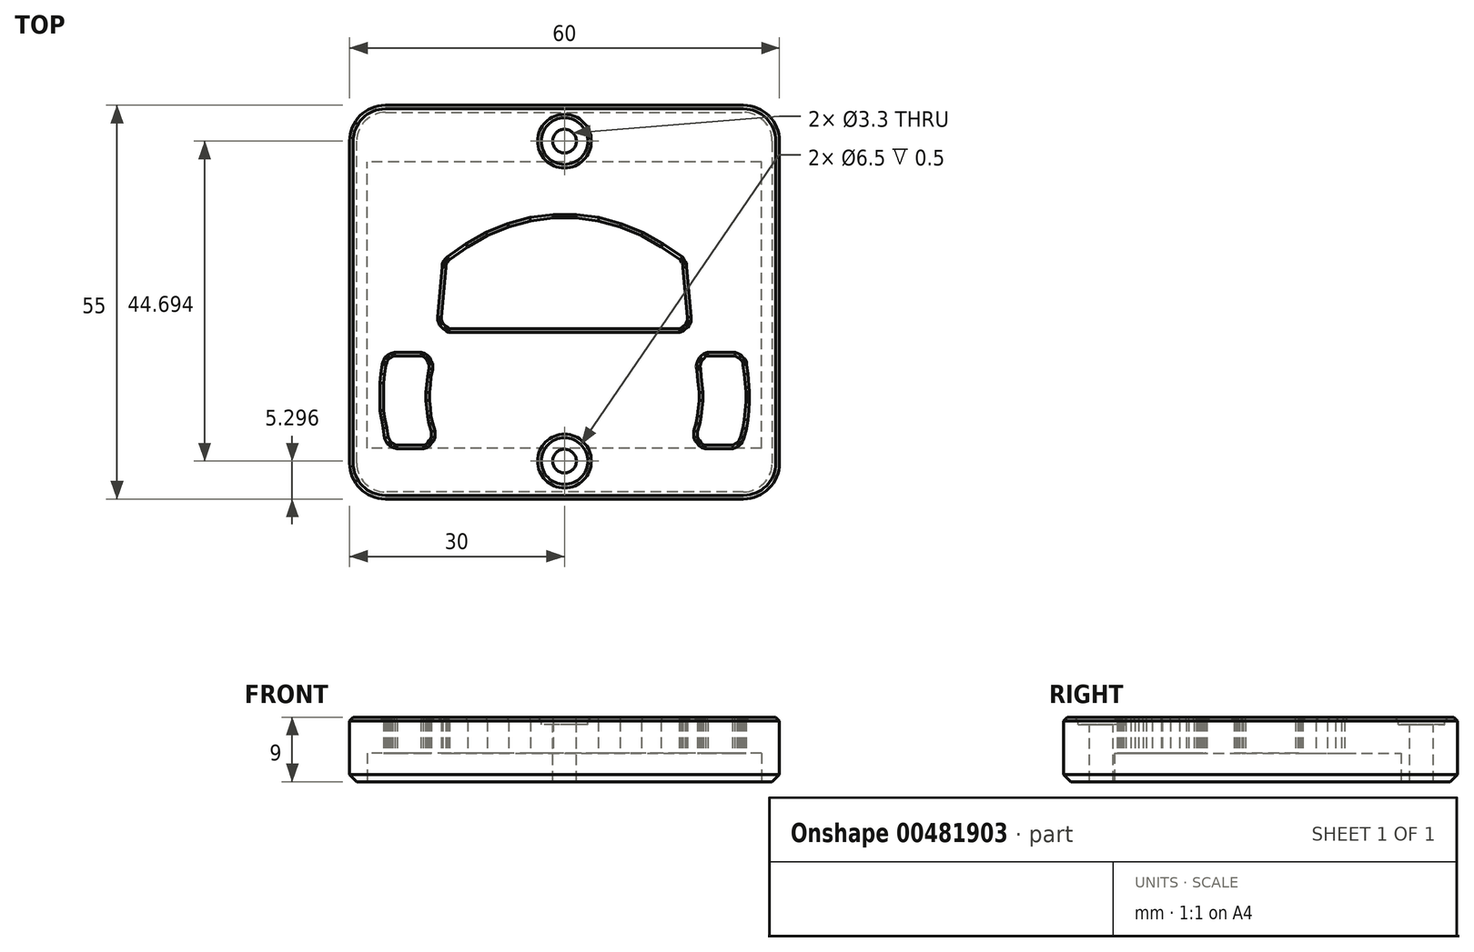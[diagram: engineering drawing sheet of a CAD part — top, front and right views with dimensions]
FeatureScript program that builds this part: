
annotation { "Feature Type Name" : "Feature", "Feature Type Description" : "" }
export const myFeature = defineFeature(function(context is Context, id is Id, definition is map)
    precondition{}
    {
        {
            var Q0;
            Q0=qCreatedBy(makeId("Top.planeOp"),FACE);
            var sketch = newSketch(context, id + "F0", { "sketchPlane" : qUnion([Q0])});
            skLineSegment(sketch, "E0.bottom", {"start": v(30, -27.5) * mm, "end": v(-30, -27.5) * mm});
            skLineSegment(sketch, "E0.top", {"start": v(30, 27.5) * mm, "end": v(-30, 27.5) * mm});
            skLineSegment(sketch, "E0.left", {"start": v(30, -27.5) * mm, "end": v(30, 27.5) * mm});
            skLineSegment(sketch, "E0.right", {"start": v(-30, -27.5) * mm, "end": v(-30, 27.5) * mm});
            skPoint(sketch, "E0.middle", {"position": v(0, 0) * mm});
            skSolve(sketch);
        }
        {
            var Q0;
            Q0 = qSketchRegion(id + "F0", true);
            extrude(context, id + "F1", {"entities" : qUnion([Q0]), "depth" : 9 * mm});
        }
        {
            var Q0;
            Q0=qCreatedBy(makeId("Top.planeOp"),FACE);
            var sketch = newSketch(context, id + "F2", { "sketchPlane" : qUnion([Q0])});
            skPoint(sketch, "E1.middle", {"position": v(0, 0) * mm});
            skLineSegment(sketch, "E2.bottom", {"start": v(27.48, -20.4) * mm, "end": v(-27.52, -20.4) * mm});
            skLineSegment(sketch, "E2.top", {"start": v(27.48, 19.6) * mm, "end": v(-27.52, 19.6) * mm});
            skLineSegment(sketch, "E2.left", {"start": v(27.48, -20.4) * mm, "end": v(27.48, 19.6) * mm});
            skLineSegment(sketch, "E2.right", {"start": v(-27.52, -20.4) * mm, "end": v(-27.52, 19.6) * mm});
            skPoint(sketch, "E2.middle", {"position": v(-0.02, -0.4) * mm});
            skSolve(sketch);
        }
        {
            var Q0;
            Q0 = qSketchRegion(id + "F2", true);
            extrude(context, id + "F3", {"entities" : qUnion([Q0]), "operationType" : NewBodyOperationType.REMOVE, "depth" : 4 * mm});
        }
        {
            var Q0;
            Q0=qCreatedBy(makeId("Top.planeOp"),FACE);
            var sketch = newSketch(context, id + "F4", { "sketchPlane" : qUnion([Q0])});
            skLineSegment(sketch, "E3", {"start": v(23.1, -20) * mm, "end": v(20.03, -20) * mm});
            skLineSegment(sketch, "E4", {"start": v(20.03, -20) * mm, "end": v(19.71, -20) * mm});
            skLineSegment(sketch, "E5", {"start": v(19.71, -20) * mm, "end": v(19.4, -19.89) * mm});
            skLineSegment(sketch, "E6", {"start": v(19.4, -19.89) * mm, "end": v(19.08, -19.68) * mm});
            skLineSegment(sketch, "E7", {"start": v(19.08, -19.68) * mm, "end": v(18.87, -19.36) * mm});
            skLineSegment(sketch, "E8", {"start": v(18.87, -19.36) * mm, "end": v(18.66, -19.15) * mm});
            skLineSegment(sketch, "E9", {"start": v(18.66, -19.15) * mm, "end": v(18.55, -18.83) * mm});
            skLineSegment(sketch, "E10", {"start": v(18.55, -18.83) * mm, "end": v(18.55, -18.4) * mm});
            skLineSegment(sketch, "E11", {"start": v(18.55, -18.4) * mm, "end": v(18.55, -18.1) * mm});
            skLineSegment(sketch, "E12", {"start": v(18.55, -18.1) * mm, "end": v(18.87, -17.03) * mm});
            skLineSegment(sketch, "E13", {"start": v(18.87, -17.03) * mm, "end": v(19.08, -15.97) * mm});
            skLineSegment(sketch, "E14", {"start": v(19.08, -15.97) * mm, "end": v(19.19, -14.8) * mm});
            skLineSegment(sketch, "E15", {"start": v(19.19, -14.8) * mm, "end": v(19.3, -13.75) * mm});
            skLineSegment(sketch, "E16", {"start": v(19.3, -13.75) * mm, "end": v(19.3, -12.59) * mm});
            skLineSegment(sketch, "E17", {"start": v(19.3, -12.59) * mm, "end": v(19.19, -11.53) * mm});
            skLineSegment(sketch, "E18", {"start": v(19.19, -11.53) * mm, "end": v(19.08, -10.37) * mm});
            skLineSegment(sketch, "E19", {"start": v(19.08, -10.37) * mm, "end": v(18.97, -9.3) * mm});
            skLineSegment(sketch, "E20", {"start": v(18.97, -9.3) * mm, "end": v(18.87, -8.99) * mm});
            skLineSegment(sketch, "E21", {"start": v(18.87, -8.99) * mm, "end": v(18.97, -8.67) * mm});
            skLineSegment(sketch, "E22", {"start": v(18.97, -8.67) * mm, "end": v(19.08, -8.36) * mm});
            skLineSegment(sketch, "E23", {"start": v(19.08, -8.36) * mm, "end": v(19.3, -8.04) * mm});
            skLineSegment(sketch, "E24", {"start": v(19.3, -8.04) * mm, "end": v(19.5, -7.83) * mm});
            skLineSegment(sketch, "E25", {"start": v(19.5, -7.83) * mm, "end": v(19.71, -7.61) * mm});
            skLineSegment(sketch, "E26", {"start": v(19.71, -7.61) * mm, "end": v(20.03, -7.5) * mm});
            skLineSegment(sketch, "E27", {"start": v(20.03, -7.5) * mm, "end": v(20.35, -7.5) * mm});
            skLineSegment(sketch, "E28", {"start": v(20.35, -7.5) * mm, "end": v(23.42, -7.5) * mm});
            skLineSegment(sketch, "E29", {"start": v(23.42, -7.5) * mm, "end": v(23.74, -7.5) * mm});
            skLineSegment(sketch, "E30", {"start": v(23.74, -7.5) * mm, "end": v(23.95, -7.61) * mm});
            skLineSegment(sketch, "E31", {"start": v(23.95, -7.61) * mm, "end": v(24.16, -7.72) * mm});
            skLineSegment(sketch, "E32", {"start": v(24.16, -7.72) * mm, "end": v(24.37, -7.83) * mm});
            skLineSegment(sketch, "E33", {"start": v(24.37, -7.83) * mm, "end": v(24.58, -8.04) * mm});
            skLineSegment(sketch, "E34", {"start": v(24.58, -8.04) * mm, "end": v(24.8, -8.25) * mm});
            skLineSegment(sketch, "E35", {"start": v(24.8, -8.25) * mm, "end": v(24.9, -8.46) * mm});
            skLineSegment(sketch, "E36", {"start": v(24.9, -8.46) * mm, "end": v(24.9, -8.78) * mm});
            skLineSegment(sketch, "E37", {"start": v(24.9, -8.78) * mm, "end": v(25.11, -10.05) * mm});
            skLineSegment(sketch, "E38", {"start": v(25.11, -10.05) * mm, "end": v(25.22, -11.32) * mm});
            skLineSegment(sketch, "E39", {"start": v(25.22, -11.32) * mm, "end": v(25.32, -12.59) * mm});
            skLineSegment(sketch, "E40", {"start": v(25.32, -12.59) * mm, "end": v(25.32, -13.86) * mm});
            skLineSegment(sketch, "E41", {"start": v(25.32, -13.86) * mm, "end": v(25.22, -15.13) * mm});
            skLineSegment(sketch, "E42", {"start": v(25.22, -15.13) * mm, "end": v(25.11, -16.4) * mm});
            skLineSegment(sketch, "E43", {"start": v(25.11, -16.4) * mm, "end": v(24.9, -17.56) * mm});
            skLineSegment(sketch, "E44", {"start": v(24.9, -17.56) * mm, "end": v(24.58, -18.83) * mm});
            skLineSegment(sketch, "E45", {"start": v(24.58, -18.83) * mm, "end": v(24.48, -19.04) * mm});
            skLineSegment(sketch, "E46", {"start": v(24.48, -19.04) * mm, "end": v(24.37, -19.25) * mm});
            skLineSegment(sketch, "E47", {"start": v(24.37, -19.25) * mm, "end": v(24.26, -19.47) * mm});
            skLineSegment(sketch, "E48", {"start": v(24.26, -19.47) * mm, "end": v(24.05, -19.68) * mm});
            skLineSegment(sketch, "E49", {"start": v(24.05, -19.68) * mm, "end": v(23.84, -19.78) * mm});
            skLineSegment(sketch, "E50", {"start": v(23.84, -19.78) * mm, "end": v(23.63, -19.89) * mm});
            skLineSegment(sketch, "E51", {"start": v(23.63, -19.89) * mm, "end": v(23.42, -20) * mm});
            skLineSegment(sketch, "E52", {"start": v(23.42, -20) * mm, "end": v(23.1, -20) * mm});
            skLineSegment(sketch, "E53", {"start": v(-23.46, -7.5) * mm, "end": v(-20.4, -7.5) * mm});
            skLineSegment(sketch, "E54", {"start": v(-20.4, -7.5) * mm, "end": v(-20.07, -7.5) * mm});
            skLineSegment(sketch, "E55", {"start": v(-20.07, -7.5) * mm, "end": v(-19.76, -7.61) * mm});
            skLineSegment(sketch, "E56", {"start": v(-19.76, -7.61) * mm, "end": v(-19.44, -7.83) * mm});
            skLineSegment(sketch, "E57", {"start": v(-19.44, -7.83) * mm, "end": v(-19.23, -8.04) * mm});
            skLineSegment(sketch, "E58", {"start": v(-19.23, -8.04) * mm, "end": v(-19.12, -8.36) * mm});
            skLineSegment(sketch, "E59", {"start": v(-19.12, -8.36) * mm, "end": v(-18.9, -8.67) * mm});
            skLineSegment(sketch, "E60", {"start": v(-18.9, -8.67) * mm, "end": v(-18.9, -8.99) * mm});
            skLineSegment(sketch, "E61", {"start": v(-18.9, -8.99) * mm, "end": v(-18.9, -9.3) * mm});
            skLineSegment(sketch, "E62", {"start": v(-18.9, -9.3) * mm, "end": v(-19.12, -10.37) * mm});
            skLineSegment(sketch, "E63", {"start": v(-19.12, -10.37) * mm, "end": v(-19.23, -11.53) * mm});
            skLineSegment(sketch, "E64", {"start": v(-19.23, -11.53) * mm, "end": v(-19.33, -12.59) * mm});
            skLineSegment(sketch, "E65", {"start": v(-19.33, -12.59) * mm, "end": v(-19.33, -13.75) * mm});
            skLineSegment(sketch, "E66", {"start": v(-19.33, -13.75) * mm, "end": v(-19.23, -14.8) * mm});
            skLineSegment(sketch, "E67", {"start": v(-19.23, -14.8) * mm, "end": v(-19.12, -15.97) * mm});
            skLineSegment(sketch, "E68", {"start": v(-19.12, -15.97) * mm, "end": v(-18.9, -17.03) * mm});
            skLineSegment(sketch, "E69", {"start": v(-18.9, -17.03) * mm, "end": v(-18.6, -18.1) * mm});
            skLineSegment(sketch, "E70", {"start": v(-18.6, -18.1) * mm, "end": v(-18.6, -18.4) * mm});
            skLineSegment(sketch, "E71", {"start": v(-18.6, -18.4) * mm, "end": v(-18.6, -18.83) * mm});
            skLineSegment(sketch, "E72", {"start": v(-18.6, -18.83) * mm, "end": v(-18.7, -19.15) * mm});
            skLineSegment(sketch, "E73", {"start": v(-18.7, -19.15) * mm, "end": v(-18.9, -19.36) * mm});
            skLineSegment(sketch, "E74", {"start": v(-18.9, -19.36) * mm, "end": v(-19.12, -19.68) * mm});
            skLineSegment(sketch, "E75", {"start": v(-19.12, -19.68) * mm, "end": v(-19.44, -19.89) * mm});
            skLineSegment(sketch, "E76", {"start": v(-19.44, -19.89) * mm, "end": v(-19.76, -20) * mm});
            skLineSegment(sketch, "E77", {"start": v(-19.76, -20) * mm, "end": v(-20.07, -20) * mm});
            skLineSegment(sketch, "E78", {"start": v(-20.07, -20) * mm, "end": v(-23.14, -20) * mm});
            skLineSegment(sketch, "E79", {"start": v(-23.14, -20) * mm, "end": v(-23.35, -20) * mm});
            skLineSegment(sketch, "E80", {"start": v(-23.35, -20) * mm, "end": v(-23.67, -19.89) * mm});
            skLineSegment(sketch, "E81", {"start": v(-23.67, -19.89) * mm, "end": v(-23.88, -19.78) * mm});
            skLineSegment(sketch, "E82", {"start": v(-23.88, -19.78) * mm, "end": v(-24.1, -19.68) * mm});
            skLineSegment(sketch, "E83", {"start": v(-24.1, -19.68) * mm, "end": v(-24.3, -19.47) * mm});
            skLineSegment(sketch, "E84", {"start": v(-24.3, -19.47) * mm, "end": v(-24.41, -19.25) * mm});
            skLineSegment(sketch, "E85", {"start": v(-24.41, -19.25) * mm, "end": v(-24.52, -19.04) * mm});
            skLineSegment(sketch, "E86", {"start": v(-24.52, -19.04) * mm, "end": v(-24.62, -18.83) * mm});
            skLineSegment(sketch, "E87", {"start": v(-24.62, -18.83) * mm, "end": v(-24.83, -17.56) * mm});
            skLineSegment(sketch, "E88", {"start": v(-24.83, -17.56) * mm, "end": v(-25.05, -16.4) * mm});
            skLineSegment(sketch, "E89", {"start": v(-25.05, -16.4) * mm, "end": v(-25.26, -15.13) * mm});
            skLineSegment(sketch, "E90", {"start": v(-25.26, -15.13) * mm, "end": v(-25.26, -13.86) * mm});
            skLineSegment(sketch, "E91", {"start": v(-25.26, -13.86) * mm, "end": v(-25.26, -12.59) * mm});
            skLineSegment(sketch, "E92", {"start": v(-25.26, -12.59) * mm, "end": v(-25.26, -11.32) * mm});
            skLineSegment(sketch, "E93", {"start": v(-25.26, -11.32) * mm, "end": v(-25.15, -10.05) * mm});
            skLineSegment(sketch, "E94", {"start": v(-25.15, -10.05) * mm, "end": v(-24.94, -8.78) * mm});
            skLineSegment(sketch, "E95", {"start": v(-24.94, -8.78) * mm, "end": v(-24.83, -8.46) * mm});
            skLineSegment(sketch, "E96", {"start": v(-24.83, -8.46) * mm, "end": v(-24.73, -8.25) * mm});
            skLineSegment(sketch, "E97", {"start": v(-24.73, -8.25) * mm, "end": v(-24.62, -8.04) * mm});
            skLineSegment(sketch, "E98", {"start": v(-24.62, -8.04) * mm, "end": v(-24.41, -7.83) * mm});
            skLineSegment(sketch, "E99", {"start": v(-24.41, -7.83) * mm, "end": v(-24.2, -7.72) * mm});
            skLineSegment(sketch, "E100", {"start": v(-24.2, -7.72) * mm, "end": v(-23.99, -7.61) * mm});
            skLineSegment(sketch, "E101", {"start": v(-23.99, -7.61) * mm, "end": v(-23.67, -7.5) * mm});
            skLineSegment(sketch, "E102", {"start": v(-23.67, -7.5) * mm, "end": v(-23.46, -7.5) * mm});
            skLineSegment(sketch, "E103", {"start": v(-17.22, -2.11) * mm, "end": v(-16.58, 4.87) * mm});
            skLineSegment(sketch, "E104", {"start": v(-16.58, 4.87) * mm, "end": v(-16.58, 4.98) * mm});
            skLineSegment(sketch, "E105", {"start": v(-16.58, 4.98) * mm, "end": v(-16.58, 5.19) * mm});
            skLineSegment(sketch, "E106", {"start": v(-16.58, 5.19) * mm, "end": v(-16.48, 5.3) * mm});
            skLineSegment(sketch, "E107", {"start": v(-16.48, 5.3) * mm, "end": v(-16.48, 5.4) * mm});
            skLineSegment(sketch, "E108", {"start": v(-16.48, 5.4) * mm, "end": v(-16.37, 5.5) * mm});
            skLineSegment(sketch, "E109", {"start": v(-16.37, 5.5) * mm, "end": v(-16.26, 5.72) * mm});
            skLineSegment(sketch, "E110", {"start": v(-16.26, 5.72) * mm, "end": v(-16.16, 5.82) * mm});
            skLineSegment(sketch, "E111", {"start": v(-16.16, 5.82) * mm, "end": v(-16.05, 5.93) * mm});
            skLineSegment(sketch, "E112", {"start": v(-16.05, 5.93) * mm, "end": v(-13.51, 7.73) * mm});
            skLineSegment(sketch, "E113", {"start": v(-13.51, 7.73) * mm, "end": v(-10.76, 9.32) * mm});
            skLineSegment(sketch, "E114", {"start": v(-10.76, 9.32) * mm, "end": v(-7.8, 10.48) * mm});
            skLineSegment(sketch, "E115", {"start": v(-7.8, 10.48) * mm, "end": v(-4.73, 11.33) * mm});
            skLineSegment(sketch, "E116", {"start": v(-4.73, 11.33) * mm, "end": v(-1.56, 11.75) * mm});
            skLineSegment(sketch, "E117", {"start": v(-1.56, 11.75) * mm, "end": v(1.62, 11.75) * mm});
            skLineSegment(sketch, "E118", {"start": v(1.62, 11.75) * mm, "end": v(4.69, 11.33) * mm});
            skLineSegment(sketch, "E119", {"start": v(4.69, 11.33) * mm, "end": v(7.76, 10.48) * mm});
            skLineSegment(sketch, "E120", {"start": v(7.76, 10.48) * mm, "end": v(10.72, 9.32) * mm});
            skLineSegment(sketch, "E121", {"start": v(10.72, 9.32) * mm, "end": v(13.47, 7.73) * mm});
            skLineSegment(sketch, "E122", {"start": v(13.47, 7.73) * mm, "end": v(16.12, 5.93) * mm});
            skLineSegment(sketch, "E123", {"start": v(16.12, 5.93) * mm, "end": v(16.22, 5.82) * mm});
            skLineSegment(sketch, "E124", {"start": v(16.22, 5.82) * mm, "end": v(16.22, 5.72) * mm});
            skLineSegment(sketch, "E125", {"start": v(16.22, 5.72) * mm, "end": v(16.33, 5.5) * mm});
            skLineSegment(sketch, "E126", {"start": v(16.33, 5.5) * mm, "end": v(16.43, 5.4) * mm});
            skLineSegment(sketch, "E127", {"start": v(16.43, 5.4) * mm, "end": v(16.54, 5.3) * mm});
            skLineSegment(sketch, "E128", {"start": v(16.54, 5.3) * mm, "end": v(16.54, 5.19) * mm});
            skLineSegment(sketch, "E129", {"start": v(16.54, 5.19) * mm, "end": v(16.54, 4.98) * mm});
            skLineSegment(sketch, "E130", {"start": v(16.54, 4.98) * mm, "end": v(16.54, 4.87) * mm});
            skLineSegment(sketch, "E131", {"start": v(16.54, 4.87) * mm, "end": v(17.17, -2.11) * mm});
            skLineSegment(sketch, "E132", {"start": v(17.17, -2.11) * mm, "end": v(17.17, -2.43) * mm});
            skLineSegment(sketch, "E133", {"start": v(17.17, -2.43) * mm, "end": v(17.17, -2.64) * mm});
            skLineSegment(sketch, "E134", {"start": v(17.17, -2.64) * mm, "end": v(16.96, -2.96) * mm});
            skLineSegment(sketch, "E135", {"start": v(16.96, -2.96) * mm, "end": v(16.86, -3.17) * mm});
            skLineSegment(sketch, "E136", {"start": v(16.86, -3.17) * mm, "end": v(16.54, -3.38) * mm});
            skLineSegment(sketch, "E137", {"start": v(16.54, -3.38) * mm, "end": v(16.33, -3.6) * mm});
            skLineSegment(sketch, "E138", {"start": v(16.33, -3.6) * mm, "end": v(16.01, -3.7) * mm});
            skLineSegment(sketch, "E139", {"start": v(16.01, -3.7) * mm, "end": v(15.7, -3.7) * mm});
            skLineSegment(sketch, "E140", {"start": v(15.7, -3.7) * mm, "end": v(-15.73, -3.7) * mm});
            skLineSegment(sketch, "E141", {"start": v(-15.73, -3.7) * mm, "end": v(-16.05, -3.7) * mm});
            skLineSegment(sketch, "E142", {"start": v(-16.05, -3.7) * mm, "end": v(-16.26, -3.6) * mm});
            skLineSegment(sketch, "E143", {"start": v(-16.26, -3.6) * mm, "end": v(-16.58, -3.38) * mm});
            skLineSegment(sketch, "E144", {"start": v(-16.58, -3.38) * mm, "end": v(-16.8, -3.17) * mm});
            skLineSegment(sketch, "E145", {"start": v(-16.8, -3.17) * mm, "end": v(-17, -2.96) * mm});
            skLineSegment(sketch, "E146", {"start": v(-17, -2.96) * mm, "end": v(-17.11, -2.64) * mm});
            skLineSegment(sketch, "E147", {"start": v(-17.11, -2.64) * mm, "end": v(-17.22, -2.43) * mm});
            skLineSegment(sketch, "E148", {"start": v(-17.22, -2.43) * mm, "end": v(-17.22, -2.11) * mm});
            skSolve(sketch);
        }
        {
            var Q0;
            Q0 = qSketchRegion(id + "F4", true);
            extrude(context, id + "F5", {"entities" : qUnion([Q0]), "operationType" : NewBodyOperationType.REMOVE, "depth" : 90 * mm});
        }
        {
            var Q0;
            Q0=makeQuery(id+"F1.opExtrude","CAP_FACE",FACE,{"disambiguationData":[OSD([sQuery(id+"F0.wireOp",EDGE,"E0.bottom"),sQuery(id+"F0.wireOp",EDGE,"E0.top"),sQuery(id+"F0.wireOp",EDGE,"E0.left"),sQuery(id+"F0.wireOp",EDGE,"E0.right")])],"isStart":false});
            var sketch = newSketch(context, id + "F6", { "sketchPlane" : qUnion([Q0])});
            skPoint(sketch, "E149", {"position": v(0, 22.49) * mm});
            skPoint(sketch, "E150", {"position": v(0, -22.2) * mm});
            skSolve(sketch);
        }
        {
            var Q0;
            Q0=sQuery(id+"F6.wireOp",VERTEX,"E149");
            var Q1;
            Q1=sQuery(id+"F6.wireOp",VERTEX,"E150");
            var Q2;
            Q2=makeQuery(id+"F1.opExtrude","SWEPT_BODY",BODY,{"disambiguationData":[OSD([sQuery(id+"F0.wireOp",EDGE,"E0.bottom"),sQuery(id+"F0.wireOp",EDGE,"E0.top"),sQuery(id+"F0.wireOp",EDGE,"E0.left"),sQuery(id+"F0.wireOp",EDGE,"E0.right")])]});
            hole(context, id + "F7", {"style" : HoleStyle.C_BORE, "endStyle" : HoleEndStyle.BLIND, "holeDiameter" : 3.3 * mm, "cBoreDiameter" : 6.5 * mm, "cBoreDepth" : 1 * mm, "holeDepth" : 13.5 * mm, "isTappedThrough" : true, "tappedDepth" : 12 * mm, "tapClearance" : 3, "startFromSketch" : true, "locations" : qUnion([Q0, Q1]), "scope" : qUnion([Q2])});
        }
        {
            var Q0;
            Q0=makeQuery(id+"F1.opExtrude","SWEPT_EDGE",EDGE,{"disambiguationData":[OSD([sQuery(id+"F0.wireOp",EDGE,"E0.top"),sQuery(id+"F0.wireOp",EDGE,"E0.right")])]});
            var Q1;
            Q1=makeQuery(id+"F1.opExtrude","SWEPT_EDGE",EDGE,{"disambiguationData":[OSD([sQuery(id+"F0.wireOp",EDGE,"E0.top"),sQuery(id+"F0.wireOp",EDGE,"E0.left")])]});
            var Q2;
            Q2=makeQuery(id+"F1.opExtrude","SWEPT_EDGE",EDGE,{"disambiguationData":[OSD([sQuery(id+"F0.wireOp",EDGE,"E0.bottom"),sQuery(id+"F0.wireOp",EDGE,"E0.left")])]});
            var Q3;
            Q3=makeQuery(id+"F1.opExtrude","SWEPT_EDGE",EDGE,{"disambiguationData":[OSD([sQuery(id+"F0.wireOp",EDGE,"E0.bottom"),sQuery(id+"F0.wireOp",EDGE,"E0.right")])]});
            fillet(context, id + "F8", {"entities" : qUnion([Q0, Q1, Q2, Q3]), "radius" : 5 * mm, "tangentPropagation" : true, "allowEdgeOverflow" : false});
        }
        {
            var Q0;
            Q0=makeQuery(id+"F1.opExtrude","CAP_EDGE",EDGE,{"disambiguationData":[OSD([sQuery(id+"F0.wireOp",EDGE,"E0.right")])],"isStart":true});
            var Q1;
            {var subQ0=sQuery(id+"F0.wireOp",EDGE,"E0.right");var subQ1=sQuery(id+"F0.wireOp",EDGE,"E0.bottom");Q1=makeQuery(id+"F8.opFillet","BLEND_EDGE",EDGE,{"blendedFrom":[makeQuery(id+"F1.opExtrude","SWEPT_EDGE",EDGE,{"disambiguationData":[OSD([subQ1,subQ0])]}),makeQuery(id+"F1.opExtrude","CAP_FACE",FACE,{"disambiguationData":[OSD([subQ1,sQuery(id+"F0.wireOp",EDGE,"E0.top"),sQuery(id+"F0.wireOp",EDGE,"E0.left"),subQ0])],"isStart":true})],"blendedInto":[makeQuery(id+"F1.opExtrude","CAP_FACE",FACE,{"disambiguationData":[OSD([subQ1,sQuery(id+"F0.wireOp",EDGE,"E0.top"),sQuery(id+"F0.wireOp",EDGE,"E0.left"),subQ0])],"isStart":true})]});}
            var Q2;
            Q2=makeQuery(id+"F1.opExtrude","CAP_EDGE",EDGE,{"disambiguationData":[OSD([sQuery(id+"F0.wireOp",EDGE,"E0.bottom")])],"isStart":true});
            var Q3;
            {var subQ0=sQuery(id+"F0.wireOp",EDGE,"E0.left");var subQ1=sQuery(id+"F0.wireOp",EDGE,"E0.bottom");Q3=makeQuery(id+"F8.opFillet","BLEND_EDGE",EDGE,{"blendedFrom":[makeQuery(id+"F1.opExtrude","SWEPT_EDGE",EDGE,{"disambiguationData":[OSD([subQ1,subQ0])]}),makeQuery(id+"F1.opExtrude","CAP_FACE",FACE,{"disambiguationData":[OSD([subQ1,sQuery(id+"F0.wireOp",EDGE,"E0.top"),subQ0,sQuery(id+"F0.wireOp",EDGE,"E0.right")])],"isStart":true})],"blendedInto":[makeQuery(id+"F1.opExtrude","CAP_FACE",FACE,{"disambiguationData":[OSD([subQ1,sQuery(id+"F0.wireOp",EDGE,"E0.top"),subQ0,sQuery(id+"F0.wireOp",EDGE,"E0.right")])],"isStart":true})]});}
            var Q4;
            Q4=makeQuery(id+"F1.opExtrude","CAP_EDGE",EDGE,{"disambiguationData":[OSD([sQuery(id+"F0.wireOp",EDGE,"E0.left")])],"isStart":true});
            var Q5;
            {var subQ0=sQuery(id+"F0.wireOp",EDGE,"E0.left");var subQ1=sQuery(id+"F0.wireOp",EDGE,"E0.top");Q5=makeQuery(id+"F8.opFillet","BLEND_EDGE",EDGE,{"blendedFrom":[makeQuery(id+"F1.opExtrude","SWEPT_EDGE",EDGE,{"disambiguationData":[OSD([subQ1,subQ0])]}),makeQuery(id+"F1.opExtrude","CAP_FACE",FACE,{"disambiguationData":[OSD([sQuery(id+"F0.wireOp",EDGE,"E0.bottom"),subQ1,subQ0,sQuery(id+"F0.wireOp",EDGE,"E0.right")])],"isStart":true})],"blendedInto":[makeQuery(id+"F1.opExtrude","CAP_FACE",FACE,{"disambiguationData":[OSD([sQuery(id+"F0.wireOp",EDGE,"E0.bottom"),subQ1,subQ0,sQuery(id+"F0.wireOp",EDGE,"E0.right")])],"isStart":true})]});}
            var Q6;
            Q6=makeQuery(id+"F1.opExtrude","CAP_EDGE",EDGE,{"disambiguationData":[OSD([sQuery(id+"F0.wireOp",EDGE,"E0.top")])],"isStart":true});
            var Q7;
            {var subQ0=sQuery(id+"F0.wireOp",EDGE,"E0.right");var subQ1=sQuery(id+"F0.wireOp",EDGE,"E0.top");Q7=makeQuery(id+"F8.opFillet","BLEND_EDGE",EDGE,{"blendedFrom":[makeQuery(id+"F1.opExtrude","SWEPT_EDGE",EDGE,{"disambiguationData":[OSD([subQ1,subQ0])]}),makeQuery(id+"F1.opExtrude","CAP_FACE",FACE,{"disambiguationData":[OSD([sQuery(id+"F0.wireOp",EDGE,"E0.bottom"),subQ1,sQuery(id+"F0.wireOp",EDGE,"E0.left"),subQ0])],"isStart":true})],"blendedInto":[makeQuery(id+"F1.opExtrude","CAP_FACE",FACE,{"disambiguationData":[OSD([sQuery(id+"F0.wireOp",EDGE,"E0.bottom"),subQ1,sQuery(id+"F0.wireOp",EDGE,"E0.left"),subQ0])],"isStart":true})]});}
            chamfer(context, id + "F9", {"entities" : qUnion([Q0, Q1, Q2, Q3, Q4, Q5, Q6, Q7]), "width" : 1 * mm, "tangentPropagation" : true});
        }
        {
            var Q0;
            Q0=makeQuery(id+"F1.opExtrude","CAP_FACE",FACE,{"disambiguationData":[OSD([sQuery(id+"F0.wireOp",EDGE,"E0.bottom"),sQuery(id+"F0.wireOp",EDGE,"E0.top"),sQuery(id+"F0.wireOp",EDGE,"E0.left"),sQuery(id+"F0.wireOp",EDGE,"E0.right")])],"isStart":false});
            chamfer(context, id + "F10", {"entities" : qUnion([Q0]), "width" : 0.5 * mm, "tangentPropagation" : true});
        }
    });
